# Revit family: 2-710-224 Telshor
name_source: partatom
category: Lighting Fixtures
revit_build: Autodesk Revit LT 2014 (Build: 20130308_1515(x64)
units: mm (PartAtom-declared; Revit-internal decimal feet)

## types (1)
- 2-710-224 Telshor
    ADA Compliant = Yes
    Apparent Load = 28 VA
    Color Filter = 16777215
    Default Elevation = 4' - 0"
    Description = 15" Comtemporary Wall Sconce
    Diffuser = Matte White Accrylic
    Dimming Lamp Color Temperature Shift = <None>
    Driver Manufacturer = Fulham
    Emit Shape Visible in Rendering = No
    Emit from Rectangle Length = 4' - 0"
    Emit from Rectangle Width = 2' - 0"
    Fixture Height = 1' - 4 15/32"
    Input Power (Watts) = 27.5
    Input Power Factor (%) = 99
    Input Voltage (Volts AC) = 120
    Junction Box = 4" Octagonal
    Lamp = 2x13W Double Twin Tube Compact Fluorescent
    Lamp Manufacturer = Sylvania
    Manufacturer = Oxygen Lighting
    Metal Finsih = Satin Finish
    Model = 2-710-224
    Photometric Web File = 2-710-224 Telshor ITL79825.IES
    Product Documentation Linkk = http://oxygenlighting.com.s3.amazonaws.com
    Tilt Angle = -90.00°
    Type Comments = Lighting - Fluorescent
    URL = http://www.oxygenlighting.com

## geometry (parser evidence)
native form markers: Sweep x1
no freeform markers — native parametric forms only
